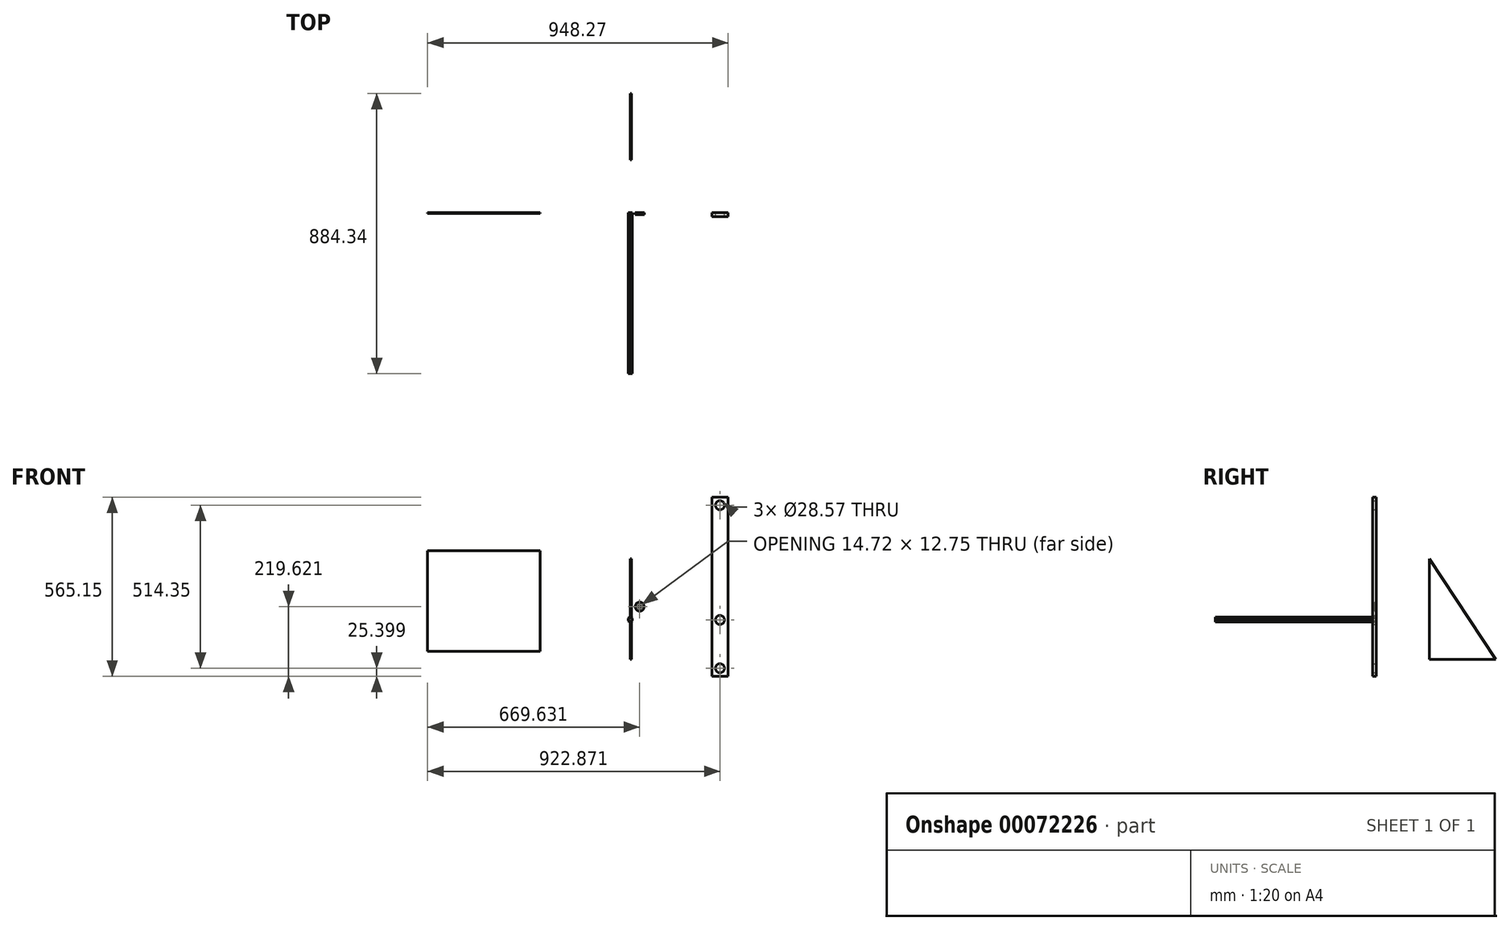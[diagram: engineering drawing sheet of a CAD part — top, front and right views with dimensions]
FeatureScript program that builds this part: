
annotation { "Feature Type Name" : "Feature", "Feature Type Description" : "" }
export const myFeature = defineFeature(function(context is Context, id is Id, definition is map)
    precondition{}
    {
        {
            var Q0;
            Q0=qCreatedBy(makeId("Front.planeOp"),FACE);
            var sketch = newSketch(context, id + "F0", { "sketchPlane" : qUnion([Q0])});
            skCircle(sketch, "E0.cCircle", {"center": v(0, 0) * mm, "radius": 6.38 * mm, "construction": true});
            skLineSegment(sketch, "E0.0", {"start": v(6.38, 3.68) * mm, "end": v(6.38, -3.68) * mm});
            skLineSegment(sketch, "E0.1", {"start": v(6.38, -3.68) * mm, "end": v(0, -7.36) * mm});
            skLineSegment(sketch, "E0.2", {"start": v(0, -7.36) * mm, "end": v(-6.38, -3.68) * mm});
            skLineSegment(sketch, "E0.3", {"start": v(-6.38, -3.68) * mm, "end": v(-6.38, 3.68) * mm});
            skLineSegment(sketch, "E0.4", {"start": v(-6.38, 3.68) * mm, "end": v(0, 7.36) * mm});
            skLineSegment(sketch, "E0.5", {"start": v(0, 7.36) * mm, "end": v(6.38, 3.68) * mm});
            skPoint(sketch, "E0.0.midPoint", {"position": v(6.38, 0) * mm});
            skSolve(sketch);
        }
        {
            var Q0;
            Q0=makeQuery(id+"F0.imprint","IMPRINT",FACE,{"disambiguationData":[TD([[makeQuery(id+"F0.imprint","IMPRINT",EDGE,{"derivedFrom":sQuery(id+"F0.wireOp",EDGE,"E0.0")}),-1.0]])]});
            extrude(context, id + "F1", {"entities" : qUnion([Q0]), "depth" : 508 * mm});
        }
        {
            var Q0;
            Q0=qCreatedBy(makeId("Front.planeOp"),FACE);
            var sketch = newSketch(context, id + "F2", { "sketchPlane" : qUnion([Q0])});
            skLineSegment(sketch, "E1", {"start": v(282.97, -1.5) * mm, "end": v(282.97, -52.3) * mm});
            skLineSegment(sketch, "E2", {"start": v(282.97, -52.3) * mm, "end": v(282.97, -77.7) * mm});
            skLineSegment(sketch, "E3", {"start": v(282.97, -77.7) * mm, "end": v(282.97, -153.9) * mm});
            skLineSegment(sketch, "E4", {"start": v(282.97, -1.5) * mm, "end": v(282.97, 49.3) * mm});
            skLineSegment(sketch, "E5", {"start": v(282.97, 49.3) * mm, "end": v(282.97, 309.66) * mm});
            skLineSegment(sketch, "E6", {"start": v(282.97, 309.66) * mm, "end": v(282.97, 360.46) * mm});
            skLineSegment(sketch, "E7", {"start": v(308.37, -179.3) * mm, "end": v(308.37, 385.86) * mm});
            skLineSegment(sketch, "E8", {"start": v(257.57, 385.86) * mm, "end": v(257.57, -179.3) * mm});
            skLineSegment(sketch, "E9", {"start": v(257.57, -179.3) * mm, "end": v(308.37, -179.3) * mm});
            skLineSegment(sketch, "E10", {"start": v(257.57, 385.86) * mm, "end": v(308.37, 385.86) * mm});
            skCircle(sketch, "E11", {"center": v(282.97, 360.46) * mm, "radius": 14.29 * mm});
            skCircle(sketch, "E12", {"center": v(282.97, -1.5) * mm, "radius": 14.29 * mm});
            skCircle(sketch, "E13", {"center": v(282.97, -153.9) * mm, "radius": 14.29 * mm});
            skSolve(sketch);
        }
        {
            var Q0;
            Q0=makeQuery(id+"F2.imprint","IMPRINT",FACE,{"disambiguationData":[TD([[makeQuery(id+"F2.imprint","IMPRINT",EDGE,{"derivedFrom":sQuery(id+"F2.wireOp",EDGE,"E7")}),1.0]])]});
            extrude(context, id + "F3", {"entities" : qUnion([Q0]), "depth" : 12.7 * mm});
        }
        {
            var Q0;
            Q0=qCreatedBy(makeId("Front.planeOp"),FACE);
            var sketch = newSketch(context, id + "F4", { "sketchPlane" : qUnion([Q0])});
            skCircle(sketch, "E14.cCircle", {"center": v(29.73, 40.33) * mm, "radius": 6.38 * mm, "construction": true});
            skLineSegment(sketch, "E14.0", {"start": v(33.41, 33.96) * mm, "end": v(26.05, 33.96) * mm});
            skLineSegment(sketch, "E14.1", {"start": v(26.05, 33.96) * mm, "end": v(22.37, 40.33) * mm});
            skLineSegment(sketch, "E14.2", {"start": v(22.37, 40.33) * mm, "end": v(26.05, 46.7) * mm});
            skLineSegment(sketch, "E14.3", {"start": v(26.05, 46.7) * mm, "end": v(33.41, 46.7) * mm});
            skLineSegment(sketch, "E14.4", {"start": v(33.41, 46.7) * mm, "end": v(37.1, 40.33) * mm});
            skLineSegment(sketch, "E14.5", {"start": v(37.1, 40.33) * mm, "end": v(33.41, 33.96) * mm});
            skPoint(sketch, "E14.0.midPoint", {"position": v(29.73, 33.96) * mm});
            skCircle(sketch, "E15", {"center": v(29.73, 40.33) * mm, "radius": 14.29 * mm});
            skSolve(sketch);
        }
        {
            var Q0;
            Q0=makeQuery(id+"F4.imprint","IMPRINT",FACE,{"disambiguationData":[TD([[makeQuery(id+"F4.imprint","IMPRINT",EDGE,{"derivedFrom":sQuery(id+"F4.wireOp",EDGE,"E14.0")}),1.0]])]});
            extrude(context, id + "F5", {"entities" : qUnion([Q0]), "depth" : 6.35 * mm});
        }
        {
            var Q0;
            Q0=qCreatedBy(makeId("Front.planeOp"),FACE);
            var sketch = newSketch(context, id + "F6", { "sketchPlane" : qUnion([Q0])});
            skLineSegment(sketch, "E16", {"start": v(-284.3, 217.33) * mm, "end": v(-284.3, -100.17) * mm});
            skLineSegment(sketch, "E17", {"start": v(-284.3, 217.33) * mm, "end": v(-639.9, 217.33) * mm});
            skLineSegment(sketch, "E18", {"start": v(-639.9, 217.33) * mm, "end": v(-639.9, -100.17) * mm});
            skLineSegment(sketch, "E19", {"start": v(-639.9, -100.17) * mm, "end": v(-284.3, -100.17) * mm});
            skSolve(sketch);
        }
        {
            var Q0;
            Q0=makeQuery(id+"F6.imprint","IMPRINT",FACE,{"disambiguationData":[TD([[makeQuery(id+"F6.imprint","IMPRINT",EDGE,{"derivedFrom":sQuery(id+"F6.wireOp",EDGE,"E16")}),-1.0]])]});
            extrude(context, id + "F7", {"entities" : qUnion([Q0]), "depth" : 3.17 * mm});
        }
        {
            var Q0;
            Q0=qCreatedBy(makeId("Right.planeOp"),FACE);
            var sketch = newSketch(context, id + "F8", { "sketchPlane" : qUnion([Q0])});
            skLineSegment(sketch, "E20", {"start": v(166.8, 192.05) * mm, "end": v(166.8, -125.45) * mm});
            skLineSegment(sketch, "E21", {"start": v(166.8, -125.45) * mm, "end": v(376.34, -125.45) * mm});
            skLineSegment(sketch, "E22", {"start": v(376.34, -125.45) * mm, "end": v(166.8, 192.05) * mm});
            skSolve(sketch);
        }
        {
            var Q0;
            Q0=makeQuery(id+"F8.imprint","IMPRINT",FACE,{"disambiguationData":[TD([[makeQuery(id+"F8.imprint","IMPRINT",EDGE,{"derivedFrom":sQuery(id+"F8.wireOp",EDGE,"E20")}),1.0]])]});
            extrude(context, id + "F9", {"entities" : qUnion([Q0]), "depth" : 3.17 * mm});
        }
    });
